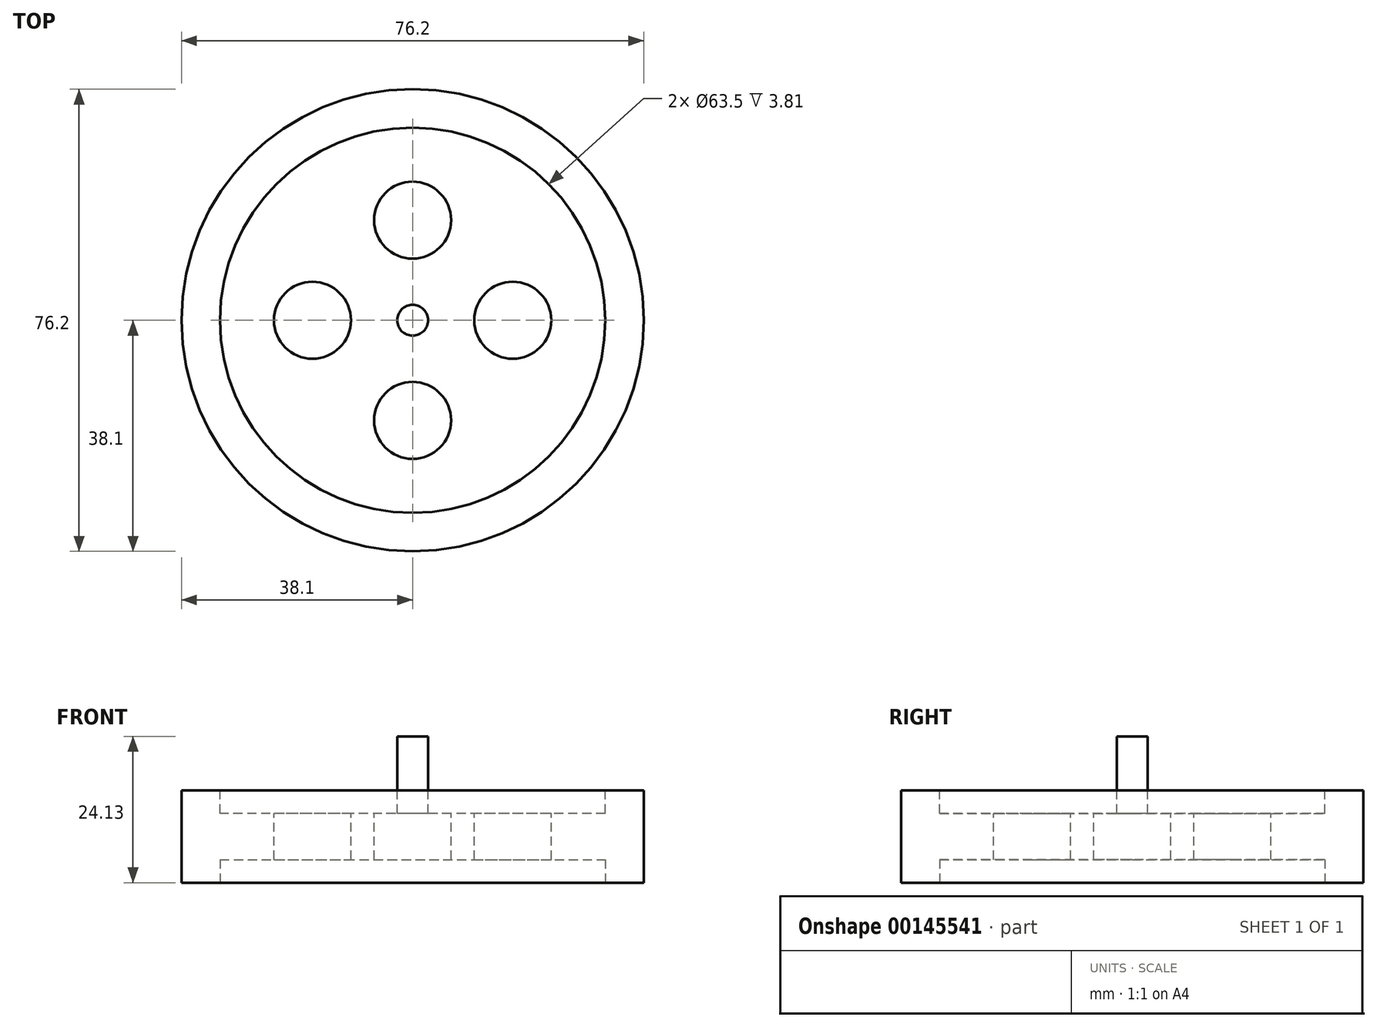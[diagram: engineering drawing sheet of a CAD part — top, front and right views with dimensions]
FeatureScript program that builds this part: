
annotation { "Feature Type Name" : "Feature", "Feature Type Description" : "" }
export const myFeature = defineFeature(function(context is Context, id is Id, definition is map)
    precondition{}
    {
        {
            var Q0;
            Q0=qCreatedBy(makeId("Top.planeOp"),FACE);
            var sketch = newSketch(context, id + "F0", { "sketchPlane" : qUnion([Q0])});
            skCircle(sketch, "E0", {"center": v(0, 0) * mm, "radius": 38.1 * mm});
            skSolve(sketch);
        }
        {
            var Q0;
            Q0=makeQuery(id+"F0.imprint","IMPRINT",FACE,{"disambiguationData":[TD([[makeQuery(id+"F0.imprint","IMPRINT",EDGE,{"derivedFrom":sQuery(id+"F0.wireOp",EDGE,"E0")}),1.0]])]});
            extrude(context, id + "F1", {"entities" : qUnion([Q0]), "depth" : 15.24 * mm});
        }
        {
            var Q0;
            Q0=makeQuery(id+"F1.opExtrude","CAP_FACE",FACE,{"disambiguationData":[OSD([sQuery(id+"F0.wireOp",EDGE,"E0")])],"isStart":false});
            var sketch = newSketch(context, id + "F2", { "sketchPlane" : qUnion([Q0])});
            skCircle(sketch, "E1", {"center": v(0, 0) * mm, "radius": 31.75 * mm});
            skSolve(sketch);
        }
        {
            var Q0;
            Q0 = qSketchRegion(id + "F2", true);
            extrude(context, id + "F3", {"entities" : qUnion([Q0]), "operationType" : NewBodyOperationType.REMOVE, "oppositeDirection" : true, "depth" : 3.8 * mm});
        }
        {
            var Q0;
            Q0=makeQuery(id+"F1.opExtrude","CAP_FACE",FACE,{"disambiguationData":[OSD([sQuery(id+"F0.wireOp",EDGE,"E0")])],"isStart":true});
            var sketch = newSketch(context, id + "F4", { "sketchPlane" : qUnion([Q0])});
            skCircle(sketch, "E2", {"center": v(0, 0) * mm, "radius": 31.75 * mm});
            skSolve(sketch);
        }
        {
            var Q0;
            Q0 = qSketchRegion(id + "F4", true);
            extrude(context, id + "F5", {"entities" : qUnion([Q0]), "operationType" : NewBodyOperationType.REMOVE, "oppositeDirection" : true, "depth" : 3.8 * mm});
        }
        {
            var Q0;
            Q0=makeQuery(id+"F3.boolean.opBoolean","COPY",FACE,{"derivedFrom":makeQuery(id+"F3.opExtrude","CAP_FACE",FACE,{"disambiguationData":[OSD([sQuery(id+"F2.wireOp",EDGE,"E1")])],"isStart":false})});
            var sketch = newSketch(context, id + "F6", { "sketchPlane" : qUnion([Q0])});
            skCircle(sketch, "E3", {"center": v(0, 16.51) * mm, "radius": 6.35 * mm});
            skCircle(sketch, "E4", {"center": v(16.51, 0) * mm, "radius": 6.35 * mm});
            skCircle(sketch, "E5", {"center": v(0, -16.51) * mm, "radius": 6.35 * mm});
            skCircle(sketch, "E6", {"center": v(-16.51, 0) * mm, "radius": 6.35 * mm});
            skSolve(sketch);
        }
        {
            var Q0;
            Q0 = qSketchRegion(id + "F6", true);
            extrude(context, id + "F7", {"entities" : qUnion([Q0]), "operationType" : NewBodyOperationType.REMOVE, "endBound" : BoundingType.THROUGH_ALL, "oppositeDirection" : true, "depth" : 25.4 * mm});
        }
        {
            var Q0;
            Q0=qCreatedBy(makeId("Front.planeOp"),FACE);
            var sketch = newSketch(context, id + "F8", { "sketchPlane" : qUnion([Q0])});
            skLineSegment(sketch, "E7", {"start": v(2.54, 24.13) * mm, "end": v(2.54, 11.43) * mm});
            skLineSegment(sketch, "E8", {"start": v(2.54, 11.43) * mm, "end": v(0, 11.43) * mm});
            skLineSegment(sketch, "E9", {"start": v(2.54, 24.13) * mm, "end": v(0, 24.13) * mm});
            skLineSegment(sketch, "E10", {"start": v(0, 24.13) * mm, "end": v(0, 11.43) * mm});
            skSolve(sketch);
        }
        {
            var Q0;
            Q0=qCreatedBy(makeId("Front.planeOp"),FACE);
            var sketch = newSketch(context, id + "F9", { "sketchPlane" : qUnion([Q0])});
            skLineSegment(sketch, "E11", {"start": v(0, 38.1) * mm, "end": v(0, 0) * mm});
            skSolve(sketch);
        }
        {
            var Q0;
            Q0=makeQuery(id+"F8.imprint","IMPRINT",FACE,{"disambiguationData":[TD([[makeQuery(id+"F8.imprint","IMPRINT",EDGE,{"derivedFrom":sQuery(id+"F8.wireOp",EDGE,"YD9mmxU7-G7mj-3vqx-lOj7-2FQzPngPymEf")}),-1.0]])]});
            var Q1;
            Q1=makeQuery(id+"F8.imprint","IMPRINT",FACE,{"disambiguationData":[TD([[makeQuery(id+"F8.imprint","IMPRINT",EDGE,{"derivedFrom":sQuery(id+"F8.wireOp",EDGE,"E7")}),-1.0]])]});
            var Q2;
            Q2=sQuery(id+"F9.wireOp",EDGE,"E11");
            revolve(context, id + "F10", {"operationType" : NewBodyOperationType.ADD, "entities" : qUnion([Q0, Q1]), "axis" : qUnion([Q2]), "revolveType" : RevolveType.FULL});
        }
    });
